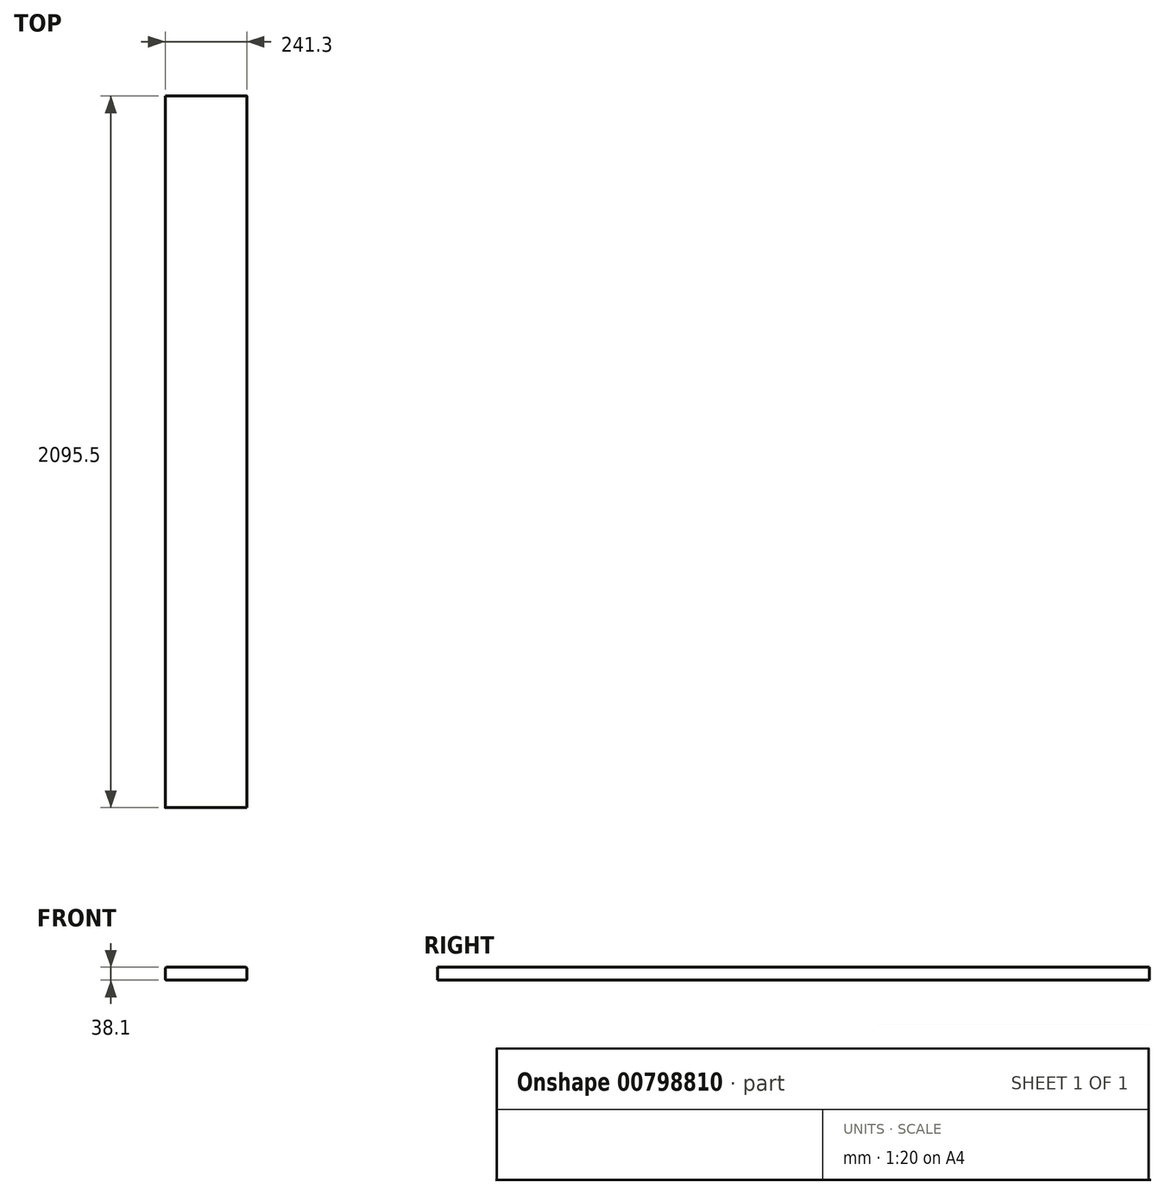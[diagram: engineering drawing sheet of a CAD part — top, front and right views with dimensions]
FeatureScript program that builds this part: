
annotation { "Feature Type Name" : "Feature", "Feature Type Description" : "" }
export const myFeature = defineFeature(function(context is Context, id is Id, definition is map)
    precondition{}
    {
        {
            var Q0;
            Q0=qCreatedBy(makeId("Front.planeOp"),FACE);
            var sketch = newSketch(context, id + "F0", { "sketchPlane" : qUnion([Q0])});
            skLineSegment(sketch, "E0.bottom", {"start": v(-115.82, 19.05) * mm, "end": v(115.82, 19.05) * mm});
            skLineSegment(sketch, "E0.top", {"start": v(-115.82, -19.05) * mm, "end": v(115.82, -19.05) * mm});
            skLineSegment(sketch, "E0.left", {"start": v(-120.65, 14.22) * mm, "end": v(-120.65, -14.22) * mm});
            skLineSegment(sketch, "E0.right", {"start": v(120.65, 14.22) * mm, "end": v(120.65, -14.22) * mm});
            skPoint(sketch, "E0.middle", {"position": v(0, 0) * mm});
            skPoint(sketch, "E1.visualSharp", {"position": v(-120.65, 19.05) * mm});
            skArc(sketch, "E1.filletArc", {"start": v(-115.82, 19.05) * mm, "mid": v(-119.24, 17.64) * mm, "end": v(-120.65, 14.22) * mm});
            skPoint(sketch, "E2.visualSharp", {"position": v(120.65, 19.05) * mm});
            skArc(sketch, "E2.filletArc", {"start": v(120.65, 14.22) * mm, "mid": v(119.24, 17.64) * mm, "end": v(115.82, 19.05) * mm});
            skPoint(sketch, "E3.visualSharp", {"position": v(120.65, -19.05) * mm});
            skArc(sketch, "E3.filletArc", {"start": v(115.82, -19.05) * mm, "mid": v(119.24, -17.64) * mm, "end": v(120.65, -14.22) * mm});
            skPoint(sketch, "E4.visualSharp", {"position": v(-120.65, -19.05) * mm});
            skArc(sketch, "E4.filletArc", {"start": v(-120.65, -14.22) * mm, "mid": v(-119.24, -17.64) * mm, "end": v(-115.82, -19.05) * mm});
            skSolve(sketch);
        }
        {
            var Q0;
            Q0=makeQuery(id+"F0.imprint","IMPRINT",FACE,{"disambiguationData":[TD([[makeQuery(id+"F0.imprint","IMPRINT",EDGE,{"derivedFrom":sQuery(id+"F0.wireOp",EDGE,"E0.bottom")}),-1.0]])]});
            extrude(context, id + "F1", {"entities" : qUnion([Q0]), "endBound" : BoundingType.SYMMETRIC, "depth" : 2095.5 * mm, "offsetDistance" : 25.4 * mm});
        }
    });
